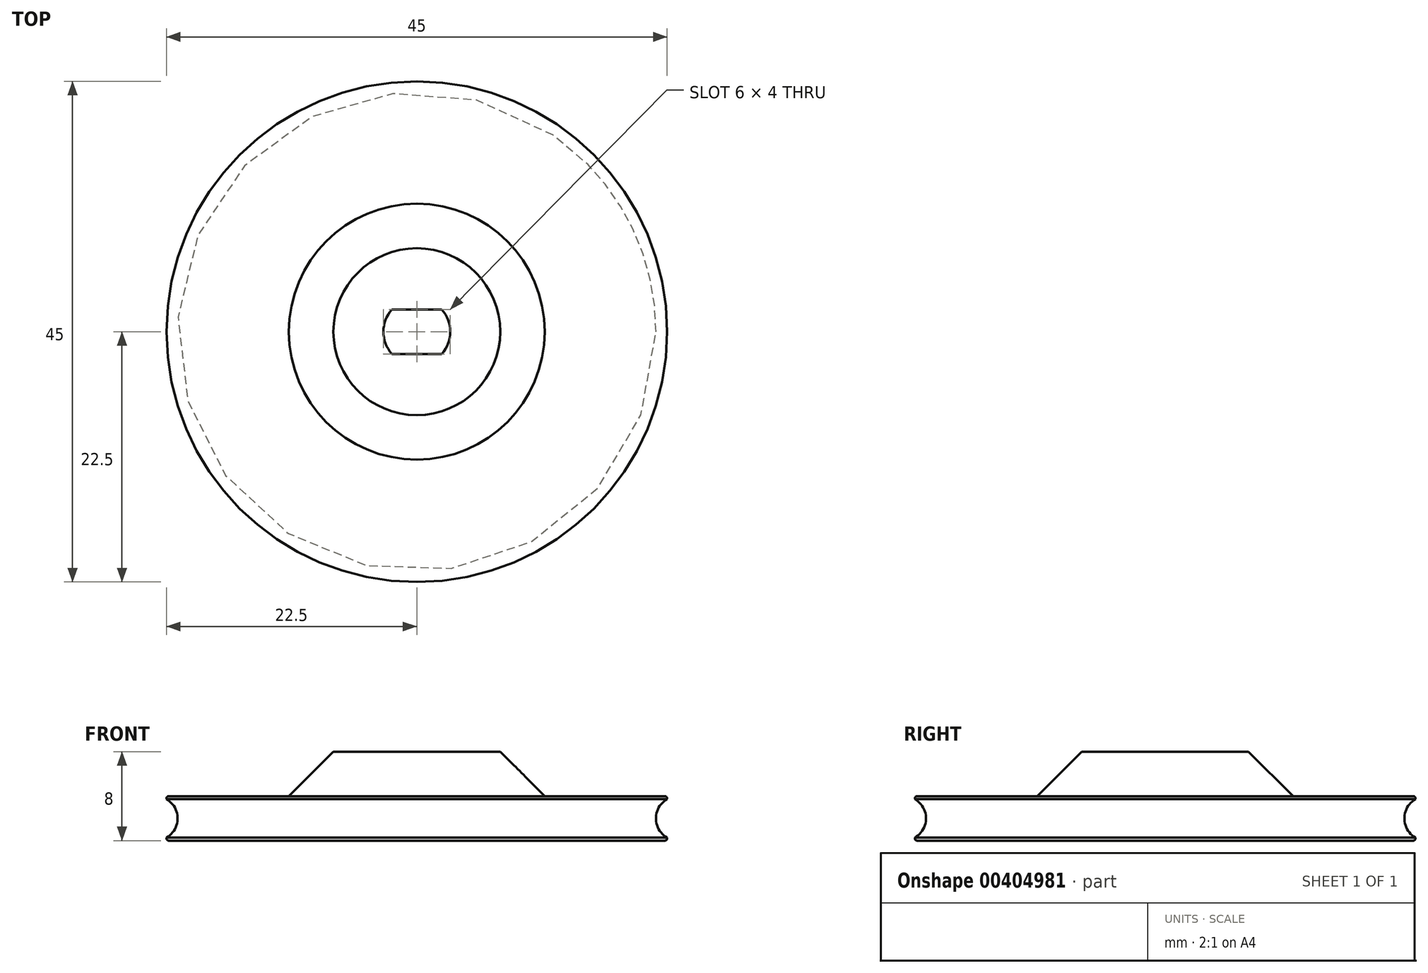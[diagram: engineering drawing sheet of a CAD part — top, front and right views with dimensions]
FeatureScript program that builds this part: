
annotation { "Feature Type Name" : "Feature", "Feature Type Description" : "" }
export const myFeature = defineFeature(function(context is Context, id is Id, definition is map)
    precondition{}
    {
        {
            var Q0;
            Q0=qCreatedBy(makeId("Top.planeOp"),FACE);
            var sketch = newSketch(context, id + "F0", { "sketchPlane" : qUnion([Q0])});
            skCircle(sketch, "E0", {"center": v(0, 0) * mm, "radius": 22.5 * mm});
            skCircle(sketch, "E1", {"center": v(0, 0) * mm, "radius": 3 * mm});
            skLineSegment(sketch, "E2", {"start": v(-2.24, -2) * mm, "end": v(2.24, -2) * mm});
            skLineSegment(sketch, "E3", {"start": v(-2.24, 2) * mm, "end": v(2.24, 2) * mm});
            skSolve(sketch);
        }
        {
            var Q0;
            Q0=makeQuery(id+"F0.imprint","IMPRINT",FACE,{"disambiguationData":[TD([[makeQuery(id+"F0.imprint","IMPRINT",EDGE,{"derivedFrom":sQuery(id+"F0.wireOp",EDGE,"E0")}),1.0]])]});
            var Q1;
            {var subQ0=sQuery(id+"F0.wireOp",EDGE,"E2");Q1=makeQuery(id+"F0.imprint","IMPRINT",FACE,{"disambiguationData":[TD([[makeQuery(id+"F0.imprint","IMPRINT",EDGE,{"derivedFrom":subQ0}),-1.0]])]});}
            var Q2;
            {var subQ0=sQuery(id+"F0.wireOp",EDGE,"E3");Q2=makeQuery(id+"F0.imprint","IMPRINT",FACE,{"disambiguationData":[TD([[makeQuery(id+"F0.imprint","IMPRINT",EDGE,{"derivedFrom":subQ0}),1.0]])]});}
            extrude(context, id + "F1", {"entities" : qUnion([Q0, Q1, Q2]), "depth" : 4 * mm});
        }
        {
            var Q0;
            Q0=qCreatedBy(makeId("Front.planeOp"),FACE);
            var sketch = newSketch(context, id + "F2", { "sketchPlane" : qUnion([Q0])});
            skLineSegment(sketch, "E4", {"start": v(0, 0) * mm, "end": v(0, 2) * mm});
            skLineSegment(sketch, "E5", {"start": v(0, 2) * mm, "end": v(-23.5, 2) * mm, "construction": true});
            skCircle(sketch, "E6", {"center": v(-23.5, 2) * mm, "radius": 2 * mm});
            skSolve(sketch);
        }
        {
            var Q0;
            Q0=makeQuery(id+"F2.imprint","IMPRINT",FACE,{"disambiguationData":[TD([[makeQuery(id+"F2.imprint","IMPRINT",EDGE,{"derivedFrom":sQuery(id+"F2.wireOp",EDGE,"E6")}),1.0]])]});
            var Q1;
            Q1=makeQuery(id+"F1.opExtrude","CAP_EDGE",EDGE,{"disambiguationData":[OSD([sQuery(id+"F0.wireOp",EDGE,"E0")])],"isStart":false});
            revolve(context, id + "F3", {"operationType" : NewBodyOperationType.REMOVE, "entities" : qUnion([Q0]), "axis" : qUnion([Q1]), "revolveType" : RevolveType.FULL, "oppositeDirection" : true});
        }
        {
            var Q0;
            Q0=makeQuery(id+"F1.opExtrude","CAP_EDGE",EDGE,{"disambiguationData":[OSD([sQuery(id+"F0.wireOp",EDGE,"E0")])],"isStart":false});
            var Q1;
            Q1=makeQuery(id+"F1.opExtrude","CAP_EDGE",EDGE,{"disambiguationData":[OSD([sQuery(id+"F0.wireOp",EDGE,"E0")])],"isStart":true});
            fillet(context, id + "F4", {"entities" : qUnion([Q0, Q1]), "radius" : .2 * mm, "tangentPropagation" : true, "allowEdgeOverflow" : false});
        }
        {
            var Q0;
            Q0=makeQuery(id+"F1.opExtrude","CAP_FACE",FACE,{"disambiguationData":[OSD([sQuery(id+"F0.wireOp",EDGE,"E0"),sQuery(id+"F0.wireOp",EDGE,"E1"),sQuery(id+"F0.wireOp",EDGE,"E2"),sQuery(id+"F0.wireOp",EDGE,"E3")])],"isStart":false});
            var sketch = newSketch(context, id + "F5", { "sketchPlane" : qUnion([Q0])});
            skCircle(sketch, "E7", {"center": v(0, 0) * mm, "radius": 12.5 * mm});
            skSolve(sketch);
        }
        {
            var Q0;
            Q0=makeQuery(id+"F5.imprint","IMPRINT",FACE,{"disambiguationData":[TD([[makeQuery(id+"F5.imprint","IMPRINT",EDGE,{"derivedFrom":sQuery(id+"F5.wireOp",EDGE,"E7")}),1.0]])]});
            extrude(context, id + "F6", {"entities" : qUnion([Q0]), "operationType" : NewBodyOperationType.ADD, "depth" : 4 * mm});
        }
        {
            var Q0;
            Q0=makeQuery(id+"F6.opExtrude","CAP_EDGE",EDGE,{"disambiguationData":[OSD([sQuery(id+"F5.wireOp",EDGE,"E7")])],"isStart":false});
            chamfer(context, id + "F7", {"entities" : qUnion([Q0]), "width" : 5 * mm, "tangentPropagation" : true});
        }
    });
